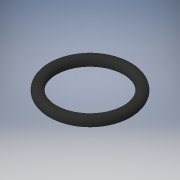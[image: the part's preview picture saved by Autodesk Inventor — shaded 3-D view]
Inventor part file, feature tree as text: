
AUTODESK INVENTOR PART (.ipt)
format: ipt  version: 2018 (Build 220112000, 112)  size: 134,656 bytes
history: native  units: mm
features: revolve x1, sketch x1
ambient origin geometry x8: Origin, YZ Plane, XZ Plane, XY Plane, X Axis, Y Axis, Z Axis, Center Point
bodies: Solid1 (feature_tree)
feature tree (2):
  revolve  "Revolution1"  [1 undecoded]
  sketch  "Sketch1"  dims[d0=7.5mm d1=2.0mm d2=90.0deg]
note: 1 required parameter value undecoded (feature->parameter linkage not recoverable at this tier; creation-order binding heuristic only, values carry confidence <= 0.55)
